# Revit family: 3010608_3010608C_TELESKOPMAST 6.0-8.5M Ø76 PL160
name_source: partatom
category: Lighting Fixtures
units: mm (PartAtom-declared; Revit-internal decimal feet)

## family parameters
Always vertical = Yes
Cut with Voids When Loaded = No
Light Source = No
Maintain Annotation Orientation = No
OmniClass Number = 23.80.70.14.21
OmniClass Title = Street and Roadway Lighting
Part Type = Normal
Room Calculation Point = No
Round Connector Dimension = Use Diameter
Shared = No
Work Plane-Based = No

## types (1)
- Teleskopmaster
    Area = 4,84 m²
    Art.nr = 3010608/3010608C
    Art.nr CombiCoat = 3010608C
    Art.nr VZN = 3010608
    Bunndiameter = Ø114
    CE-godkjent = Ja
    Category = Teleskopmaster
    Center of Gravity = X: -0,003 mm Y: 1,047 mm Z: 3730,840 mm
    Default Elevation = 0 mm  [stored 0 ft]
    Density = 7632,48 kg/m³
    Description = TELESKOPMAST 6.0-8.5M Ø76 PL160
    Design Status = 1
    Designer = khk
    EL nr CombiCoat = 3640807
    El nr = 3640106/3640118
    El nr VZN = 3640803
    Filnamn-VO = Standard
    Filnavn = TELESKOPMAST 6.0-8.5M Ø76 PL160
    Fotplate C/C bolter = 160mm
    Fundament = Fotplate
    Lyspunkthoyde = 6,0-8,5m
    Manufacturer = Vik Ørsta AS
    Mass = 59,64 kg
    Materialkvalitet = S355
    Model = 3010608_3010608C
    Part Number = L10184
    Requested Accuracy = Low
    Revision Number = -
    Size = 0,0,0
    Sti&Filnamn-VO = Standard
    Title = TELESKOPMAST 6.0-8.5M Ø76 PL160
    Toppdiameter = Ø76
    Volume = 0,01 m³

note: [stored X ft] marks values corroborated as IEEE doubles in the binary element streams (Revit-internal decimal feet)

## geometry (parser evidence)
native form markers: Sweep x2
no freeform markers — native parametric forms only
